# Revit family: AFX-Sia-LED_Vanity-1
name_source: partatom
category: Lighting Fixtures
units: mm (PartAtom-declared; Revit-internal decimal feet)

## family parameters
Cut with Voids When Loaded = No
Host = Face
Light Source = Yes
Part Type = Normal
Room Calculation Point = No
Round Connector Dimension = Use Diameter
Shared = No

## types (1)
- SIAV2407LAJUDBK
    Apparent Load = 0 VA
    Assembly Code = D5020200
    Body Finish = AFX - Black Steel
    Color Filter = 16777215
    Colour Rendering Index = 80
    Default Elevation = 48"
    Depth = 4"
    Description = LED Vanity - 23 1/4"H x 6 1/2"W x 4"D
    Diffuser Finish = AFX - White Acrylic
    Dimming Lamp Color Temperature Shift = <None>
    Emit Shape Visible in Rendering = No
    Emit from Rectangle Length = 20"
    Emit from Rectangle Width = 6"
    Height = 6 1/2"
    Housing Finish = AFX - Black Steel
    Keynote = 12500
    Length = 23 1/4"
    Manufacturer = AFX Inc
    Model = SIAV2407LAJUDBK
    Photometric Web File = SIAV2407LAJUDBK_3000K_IES.IES
    Product Documentation Link = https://www.afxinc.com
    Revit File Built By = https://servex-us.com
    Sustainability = https://lamprecycle.org
    Tilt Angle = 0.00°
    Type Comments = Sia
    URL = https://www.afxinc.com
    Voltage = 120 V
    Wattage Comments = 35W

## geometry (parser evidence)
native form markers: Sweep x5
no freeform markers — native parametric forms only
